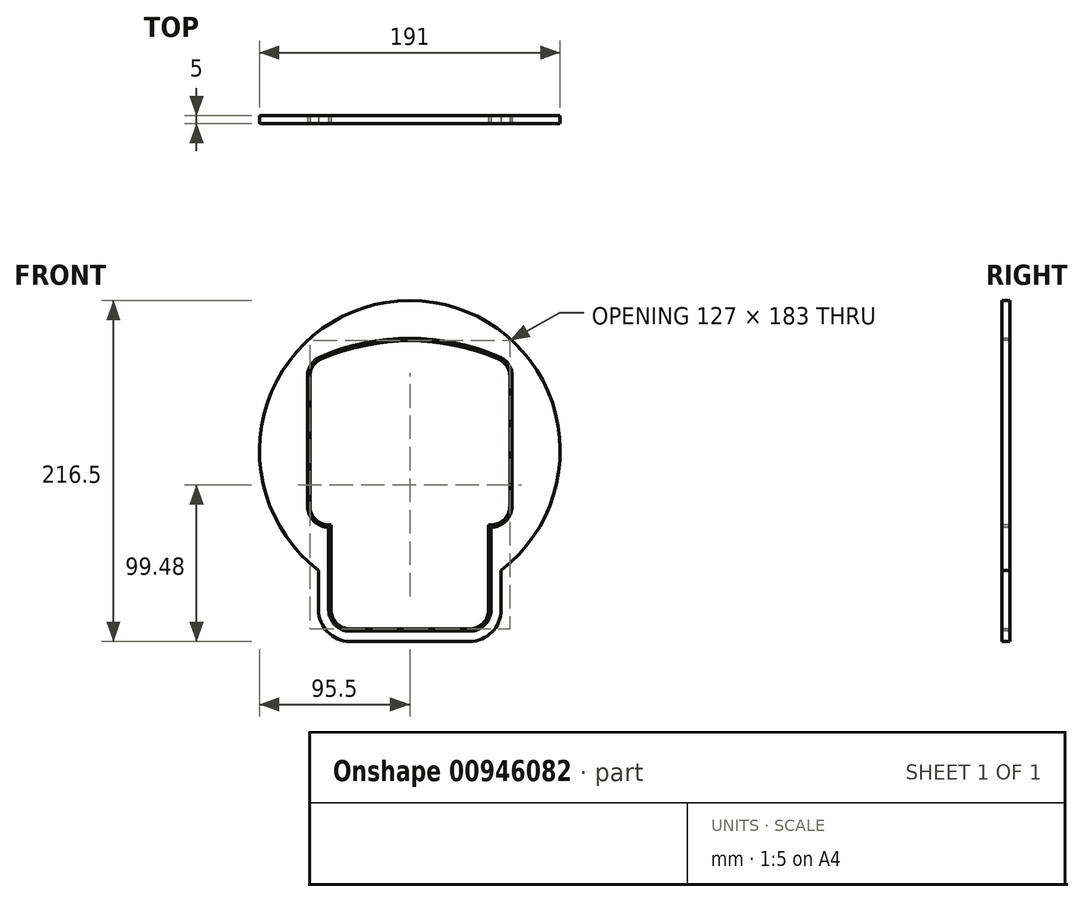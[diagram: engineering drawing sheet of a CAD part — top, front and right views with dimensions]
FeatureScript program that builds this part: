
annotation { "Feature Type Name" : "Feature", "Feature Type Description" : "" }
export const myFeature = defineFeature(function(context is Context, id is Id, definition is map)
    precondition{}
    {
        {
            var Q0;
            Q0=qCreatedBy(makeId("Front.planeOp"),FACE);
            var sketch = newSketch(context, id + "F0", { "sketchPlane" : qUnion([Q0])});
            skLineSegment(sketch, "E0.top", {"start": v(-38, -113.02) * mm, "end": v(38, -113.02) * mm});
            skLineSegment(sketch, "E0.left", {"start": v(-50, -47.02) * mm, "end": v(-50, -101.02) * mm});
            skLineSegment(sketch, "E0.right", {"start": v(50, -47.02) * mm, "end": v(50, -101.02) * mm});
            skLineSegment(sketch, "E1.top", {"start": v(51.5, -47.02) * mm, "end": v(50, -47.02) * mm});
            skLineSegment(sketch, "E1.left", {"start": v(63.5, 47.34) * mm, "end": v(63.5, -35.02) * mm});
            skLineSegment(sketch, "E1.right", {"start": v(-63.5, 47.34) * mm, "end": v(-63.5, -35.02) * mm});
            skArc(sketch, "E2", {"start": v(56.26, 58.35) * mm, "mid": v(0, 69.98) * mm, "end": v(-56.26, 58.35) * mm});
            skArc(sketch, "E3.filletArc", {"start": v(-56.26, 58.35) * mm, "mid": v(-61.53, 53.93) * mm, "end": v(-63.5, 47.34) * mm});
            skArc(sketch, "E4.filletArc", {"start": v(63.5, 47.34) * mm, "mid": v(61.53, 53.93) * mm, "end": v(56.26, 58.35) * mm});
            skPoint(sketch, "E5.visualSharp", {"position": v(63.5, -47.02) * mm});
            skArc(sketch, "E5.filletArc", {"start": v(51.5, -47.02) * mm, "mid": v(59.99, -43.5) * mm, "end": v(63.5, -35.02) * mm});
            skPoint(sketch, "E6.visualSharp", {"position": v(-63.5, -47.02) * mm});
            skArc(sketch, "E6.filletArc", {"start": v(-63.5, -35.02) * mm, "mid": v(-59.99, -43.5) * mm, "end": v(-51.5, -47.02) * mm});
            skPoint(sketch, "E7.visualSharp", {"position": v(-50, -113.02) * mm});
            skArc(sketch, "E7.filletArc", {"start": v(-50, -101.02) * mm, "mid": v(-46.49, -109.5) * mm, "end": v(-38, -113.02) * mm});
            skPoint(sketch, "E8.visualSharp", {"position": v(50, -113.02) * mm});
            skArc(sketch, "E8.filletArc", {"start": v(38, -113.02) * mm, "mid": v(46.49, -109.5) * mm, "end": v(50, -101.02) * mm});
            skLineSegment(sketch, "E9.trimOffspring", {"start": v(-50, -47.02) * mm, "end": v(-51.5, -47.02) * mm});
            skLineSegment(sketch, "E10.0", {"start": v(65, 47.34) * mm, "end": v(65, -35.02) * mm});
            skArc(sketch, "E10.1", {"start": v(-65, -35.02) * mm, "mid": v(-61.05, -44.57) * mm, "end": v(-51.5, -48.52) * mm});
            skLineSegment(sketch, "E10.2", {"start": v(-65, 47.34) * mm, "end": v(-65, -35.02) * mm});
            skArc(sketch, "E10.3", {"start": v(-56.85, 59.73) * mm, "mid": v(-62.78, 54.75) * mm, "end": v(-65, 47.34) * mm});
            skArc(sketch, "E10.4", {"start": v(56.85, 59.73) * mm, "mid": v(0, 71.48) * mm, "end": v(-56.85, 59.73) * mm});
            skLineSegment(sketch, "E10.5", {"start": v(-51.5, -48.52) * mm, "end": v(-51.5, -101.02) * mm});
            skArc(sketch, "E10.6", {"start": v(65, 47.34) * mm, "mid": v(62.78, 54.75) * mm, "end": v(56.85, 59.73) * mm});
            skArc(sketch, "E10.7", {"start": v(-51.5, -101.02) * mm, "mid": v(-47.55, -110.57) * mm, "end": v(-38, -114.52) * mm});
            skLineSegment(sketch, "E10.8", {"start": v(-38, -114.52) * mm, "end": v(38, -114.52) * mm});
            skArc(sketch, "E10.9", {"start": v(38, -114.52) * mm, "mid": v(47.55, -110.57) * mm, "end": v(51.5, -101.02) * mm});
            skLineSegment(sketch, "E10.10", {"start": v(51.5, -48.52) * mm, "end": v(51.5, -101.02) * mm});
            skArc(sketch, "E10.11", {"start": v(51.5, -48.52) * mm, "mid": v(61.05, -44.57) * mm, "end": v(65, -35.02) * mm});
            skSolve(sketch);
        }
        {
            var Q0;
            Q0=qCreatedBy(makeId("Front.planeOp"),FACE);
            var sketch = newSketch(context, id + "F1", { "sketchPlane" : qUnion([Q0])});
            skLineSegment(sketch, "E11.top", {"start": v(-38, -113) * mm, "end": v(38, -113) * mm});
            skLineSegment(sketch, "E11.left", {"start": v(-50, -71.8) * mm, "end": v(-50, -101) * mm});
            skLineSegment(sketch, "E11.right", {"start": v(50, -71.8) * mm, "end": v(50, -101) * mm});
            skArc(sketch, "E12.filletArc", {"start": v(-50, -101) * mm, "mid": v(-46.49, -109.48) * mm, "end": v(-38, -113) * mm});
            skArc(sketch, "E13.filletArc", {"start": v(38, -113) * mm, "mid": v(46.49, -109.48) * mm, "end": v(50, -101) * mm});
            skArc(sketch, "E14", {"start": v(50, -71.8) * mm, "mid": v(0, 87.5) * mm, "end": v(-50, -71.8) * mm});
            skLineSegment(sketch, "E15.0", {"start": v(58, -75.87) * mm, "end": v(58, -101) * mm});
            skLineSegment(sketch, "E15.1", {"start": v(-58, -75.87) * mm, "end": v(-58, -101) * mm});
            skArc(sketch, "E15.2", {"start": v(-58, -101) * mm, "mid": v(-52.14, -115.14) * mm, "end": v(-38, -121) * mm});
            skArc(sketch, "E15.3", {"start": v(58, -75.87) * mm, "mid": v(0, 95.5) * mm, "end": v(-58, -75.87) * mm});
            skLineSegment(sketch, "E15.4", {"start": v(-38, -121) * mm, "end": v(38, -121) * mm});
            skArc(sketch, "E15.5", {"start": v(38, -121) * mm, "mid": v(52.14, -115.14) * mm, "end": v(58, -101) * mm});
            skSolve(sketch);
        }
        {
            var Q0;
            Q0=makeQuery(id+"F1.imprint","IMPRINT",FACE,{"disambiguationData":[TD([[makeQuery(id+"F1.imprint","IMPRINT",EDGE,{"derivedFrom":sQuery(id+"F1.wireOp",EDGE,"E11.top")}),-1.0]])]});
            var Q1;
            Q1=makeQuery(id+"F1.imprint","IMPRINT",FACE,{"disambiguationData":[TD([[makeQuery(id+"F1.imprint","IMPRINT",EDGE,{"derivedFrom":sQuery(id+"F1.wireOp",EDGE,"E11.top")}),1.0]])]});
            var Q2;
            Q2 = qSketchRegion(id + "F0", true);
            extrude(context, id + "F2", {"entities" : qUnion([Q0, Q1, Q2]), "oppositeDirection" : true, "depth" : 5 * mm, "offsetDistance" : 25 * mm});
        }
    });
